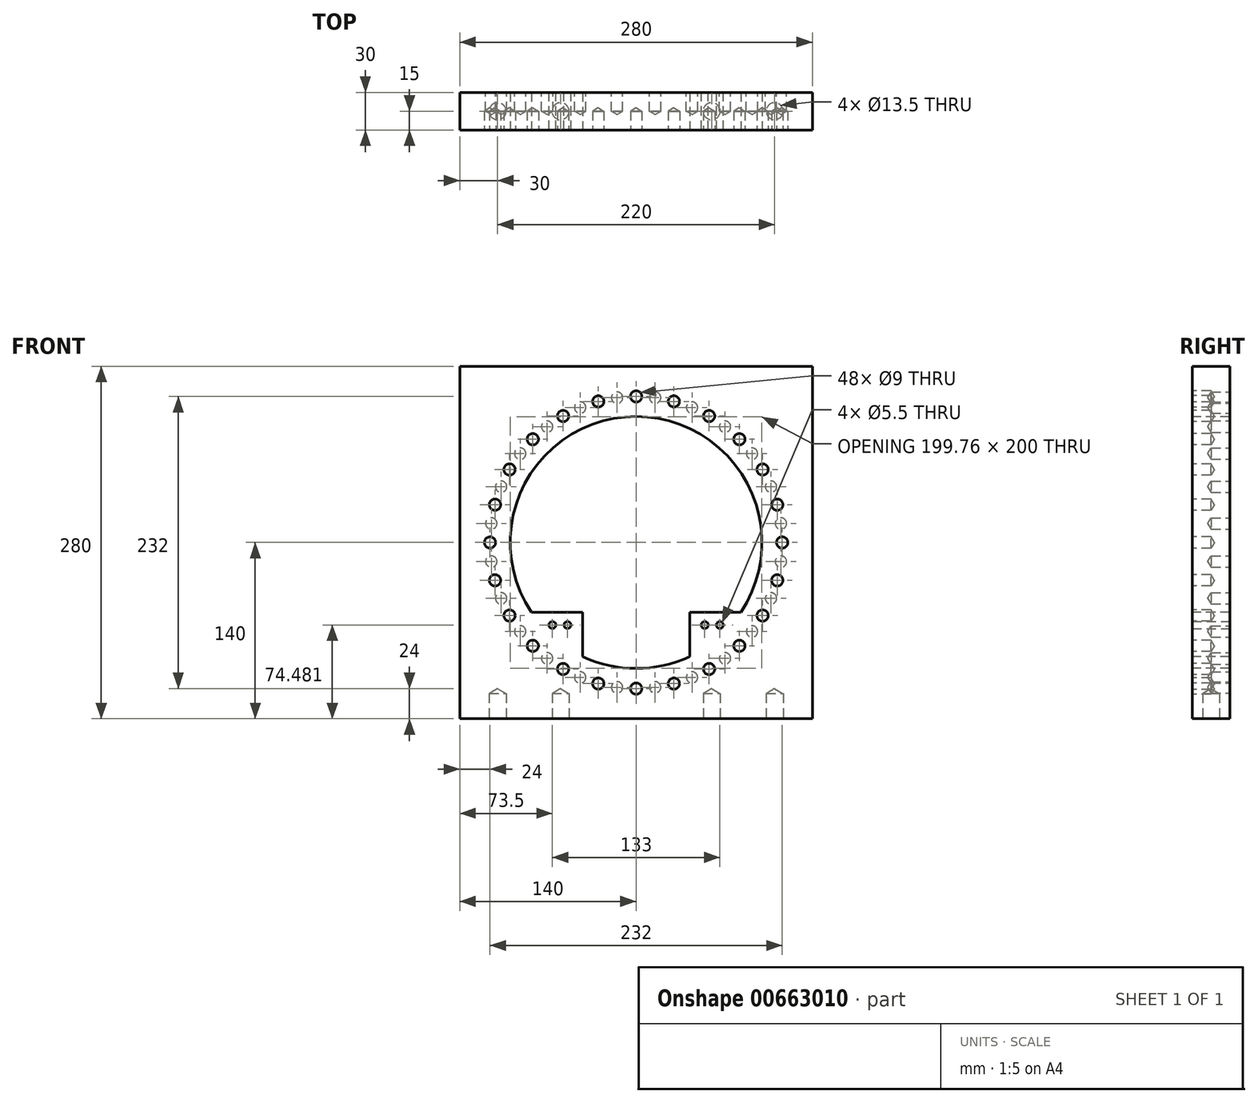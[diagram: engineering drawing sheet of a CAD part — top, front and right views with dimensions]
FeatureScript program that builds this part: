
annotation { "Feature Type Name" : "Feature", "Feature Type Description" : "" }
export const myFeature = defineFeature(function(context is Context, id is Id, definition is map)
    precondition{}
    {
        {
            var Q0;
            Q0=qCreatedBy(makeId("Front.planeOp"),FACE);
            var sketch = newSketch(context, id + "F0", { "sketchPlane" : qUnion([Q0])});
            skLineSegment(sketch, "E0.bottom", {"start": v(140, -140) * mm, "end": v(-140, -140) * mm});
            skLineSegment(sketch, "E0.top", {"start": v(140, 140) * mm, "end": v(-140, 140) * mm});
            skLineSegment(sketch, "E0.left", {"start": v(140, -140) * mm, "end": v(140, 140) * mm});
            skLineSegment(sketch, "E0.right", {"start": v(-140, -140) * mm, "end": v(-140, 140) * mm});
            skPoint(sketch, "E0.middle", {"position": v(0, 0) * mm});
            skCircle(sketch, "E1", {"center": v(0, 0) * mm, "radius": 100 * mm});
            skCircle(sketch, "E2", {"center": v(0, 0) * mm, "radius": 127 * mm, "construction": true});
            skSolve(sketch);
        }
        {
            var Q0;
            Q0=makeQuery(id+"F0.imprint","IMPRINT",FACE,{"disambiguationData":[TD([[makeQuery(id+"F0.imprint","IMPRINT",EDGE,{"derivedFrom":sQuery(id+"F0.wireOp",EDGE,"E0.bottom")}),-1.0]])]});
            var Q1;
            Q1=makeQuery(id+"F0.imprint","IMPRINT",FACE,{"disambiguationData":[TD([[makeQuery(id+"F0.imprint","IMPRINT",EDGE,{"derivedFrom":sQuery(id+"F0.wireOp",EDGE,"E1")}),1.0]])]});
            extrude(context, id + "F1", {"entities" : qUnion([Q0, Q1]), "depth" : 30 * mm, "offsetDistance" : 25 * mm});
        }
        {
            var Q0;
            Q0=makeQuery(id+"F1.opExtrude","SWEPT_FACE",FACE,{"disambiguationData":[OSD([sQuery(id+"F0.wireOp",EDGE,"E0.bottom")])]});
            var sketch = newSketch(context, id + "F2", { "sketchPlane" : qUnion([Q0])});
            skPoint(sketch, "E3", {"position": v(-110, 15) * mm});
            skPoint(sketch, "E3.positionSnap0", {"position": v(-140, 15) * mm});
            skPoint(sketch, "E4", {"position": v(110, 15) * mm});
            skPoint(sketch, "E5", {"position": v(60, 15) * mm});
            skPoint(sketch, "E6", {"position": v(-60, 15) * mm});
            skLineSegment(sketch, "E7", {"start": v(140, 15) * mm, "end": v(110, 15) * mm, "construction": true});
            skLineSegment(sketch, "E8", {"start": v(110, 15) * mm, "end": v(60, 15) * mm, "construction": true});
            skLineSegment(sketch, "E9", {"start": v(60, 15) * mm, "end": v(-60, 15) * mm, "construction": true});
            skLineSegment(sketch, "E10", {"start": v(-60, 15) * mm, "end": v(-110, 15) * mm, "construction": true});
            skLineSegment(sketch, "E11", {"start": v(-110, 15) * mm, "end": v(-140, 15) * mm, "construction": true});
            skSolve(sketch);
        }
        {
            var Q0;
            Q0=sQuery(id+"F2.wireOp",VERTEX,"E4");
            var Q1;
            Q1=sQuery(id+"F2.wireOp",VERTEX,"E5");
            var Q2;
            Q2=sQuery(id+"F2.wireOp",VERTEX,"E6");
            var Q3;
            Q3=sQuery(id+"F2.wireOp",VERTEX,"E3");
            var Q4;
            Q4=makeQuery(id+"F1.opExtrude","SWEPT_BODY",BODY,{"disambiguationData":[OSD([sQuery(id+"F0.wireOp",EDGE,"E0.bottom"),sQuery(id+"F0.wireOp",EDGE,"E0.top"),sQuery(id+"F0.wireOp",EDGE,"E0.left"),sQuery(id+"F0.wireOp",EDGE,"E0.right"),sQuery(id+"F0.wireOp",EDGE,"E1")])]});
            hole(context, id + "F3", {"style" : HoleStyle.SIMPLE, "endStyle" : HoleEndStyle.BLIND, "standardTappedOrClearance" : lookupTablePath({ "fit" : "Normal", "standard" : "ISO", "size" : "M12", "type" : "Clearance" }), "standardBlindInLast" : lookupTablePath({ "fit" : "Normal", "standard" : "ISO", "engagement" : "75%", "pitch" : "1.75 mm", "size" : "M12", "type" : "Clearance & tapped" }), "holeDiameter" : 13.5 * mm, "majorDiameter" : 5 * mm, "holeDepth" : 20 * mm, "isTappedThrough" : true, "tappedDepth" : 12 * mm, "tapClearance" : 3, "locations" : qUnion([Q0, Q1, Q2, Q3]), "scope" : qUnion([Q4])});
        }
        {
            var Q0;
            Q0=makeQuery(id+"F1.opExtrude","CAP_FACE",FACE,{"disambiguationData":[OSD([sQuery(id+"F0.wireOp",EDGE,"E0.bottom"),sQuery(id+"F0.wireOp",EDGE,"E0.top"),sQuery(id+"F0.wireOp",EDGE,"E0.left"),sQuery(id+"F0.wireOp",EDGE,"E0.right")])],"isStart":false});
            var sketch = newSketch(context, id + "F4", { "sketchPlane" : qUnion([Q0])});
            skLineSegment(sketch, "E12", {"start": v(42.5, -90.52) * mm, "end": v(42.5, -55.52) * mm});
            skLineSegment(sketch, "E13", {"start": v(42.5, -55.52) * mm, "end": v(83.17, -55.52) * mm});
            skLineSegment(sketch, "E14", {"start": v(-83.17, -55.52) * mm, "end": v(-42.5, -55.52) * mm});
            skLineSegment(sketch, "E15", {"start": v(-42.5, -55.52) * mm, "end": v(42.5, -55.52) * mm, "construction": true});
            skLineSegment(sketch, "E16", {"start": v(-42.5, -55.52) * mm, "end": v(-42.5, -90.52) * mm});
            skLineSegment(sketch, "E17", {"start": v(0, -55.52) * mm, "end": v(0, -85.52) * mm, "construction": true});
            skLineSegment(sketch, "E18", {"start": v(-42.5, -85.52) * mm, "end": v(0, -85.52) * mm, "construction": true});
            skLineSegment(sketch, "E19", {"start": v(0, -85.52) * mm, "end": v(42.5, -85.52) * mm, "construction": true});
            skArc(sketch, "E20", {"start": v(-42.5, -90.52) * mm, "mid": v(0, -100) * mm, "end": v(42.5, -90.52) * mm});
            skArc(sketch, "E21", {"start": v(42.5, -90.52) * mm, "mid": v(65.23, -75.8) * mm, "end": v(83.17, -55.52) * mm, "construction": true});
            skLineSegment(sketch, "E22", {"start": v(83.17, -55.52) * mm, "end": v(83.17, -55.52) * mm});
            skArc(sketch, "E23", {"start": v(-83.17, -55.52) * mm, "mid": v(-65.23, -75.8) * mm, "end": v(-42.5, -90.52) * mm, "construction": true});
            skLineSegment(sketch, "E24", {"start": v(0, 0) * mm, "end": v(0, -55.52) * mm, "construction": true});
            skArc(sketch, "E25", {"start": v(83.17, -55.52) * mm, "mid": v(0, 100) * mm, "end": v(-83.17, -55.52) * mm});
            skSolve(sketch);
        }
        {
            var Q0;
            Q0=makeQuery(id+"F4.imprint","IMPRINT",FACE,{"disambiguationData":[TD([[makeQuery(id+"F4.imprint","IMPRINT",EDGE,{"derivedFrom":sQuery(id+"F4.wireOp",EDGE,"E12")}),1.0]])]});
            extrude(context, id + "F5", {"entities" : qUnion([Q0]), "operationType" : NewBodyOperationType.REMOVE, "endBound" : BoundingType.THROUGH_ALL, "oppositeDirection" : true, "depth" : 25 * mm, "offsetDistance" : 25 * mm});
        }
        {
            var Q0;
            Q0=makeQuery(id+"F1.opExtrude","CAP_FACE",FACE,{"disambiguationData":[OSD([sQuery(id+"F0.wireOp",EDGE,"E0.bottom"),sQuery(id+"F0.wireOp",EDGE,"E0.top"),sQuery(id+"F0.wireOp",EDGE,"E0.left"),sQuery(id+"F0.wireOp",EDGE,"E0.right")])],"isStart":false});
            var sketch = newSketch(context, id + "F6", { "sketchPlane" : qUnion([Q0])});
            skCircle(sketch, "E26", {"center": v(0, 0) * mm, "radius": 116 * mm, "construction": true});
            skPoint(sketch, "E27", {"position": v(0, 116) * mm});
            skPoint(sketch, "E28.1.0", {"position": v(-30.02, 112.05) * mm});
            skPoint(sketch, "E28.2.0", {"position": v(-58, 100.46) * mm});
            skPoint(sketch, "E28.3.0", {"position": v(-82.02, 82.02) * mm});
            skPoint(sketch, "E28.4.0", {"position": v(-100.46, 58) * mm});
            skPoint(sketch, "E28.5.0", {"position": v(-112.05, 30.02) * mm});
            skPoint(sketch, "E28.6.0", {"position": v(-116, 0) * mm});
            skPoint(sketch, "E28.7.0", {"position": v(-112.05, -30.02) * mm});
            skPoint(sketch, "E28.8.0", {"position": v(-100.46, -58) * mm});
            skPoint(sketch, "E28.9.0", {"position": v(-82.02, -82.02) * mm});
            skPoint(sketch, "E28.10.0", {"position": v(-58, -100.46) * mm});
            skPoint(sketch, "E28.11.0", {"position": v(-30.02, -112.05) * mm});
            skPoint(sketch, "E28.12.0", {"position": v(0, -116) * mm});
            skPoint(sketch, "E28.13.0", {"position": v(30.02, -112.05) * mm});
            skPoint(sketch, "E28.14.0", {"position": v(58, -100.46) * mm});
            skPoint(sketch, "E28.15.0", {"position": v(82.02, -82.02) * mm});
            skPoint(sketch, "E28.16.0", {"position": v(100.46, -58) * mm});
            skPoint(sketch, "E28.17.0", {"position": v(112.05, -30.02) * mm});
            skPoint(sketch, "E28.18.0", {"position": v(116, 0) * mm});
            skPoint(sketch, "E28.19.0", {"position": v(112.05, 30.02) * mm});
            skPoint(sketch, "E28.20.0", {"position": v(100.46, 58) * mm});
            skPoint(sketch, "E28.21.0", {"position": v(82.02, 82.02) * mm});
            skPoint(sketch, "E28.22.0", {"position": v(58, 100.46) * mm});
            skPoint(sketch, "E28.23.0", {"position": v(30.02, 112.05) * mm});
            skSolve(sketch);
        }
        {
            var Q0;
            Q0=sQuery(id+"F6.wireOp",VERTEX,"E27");
            var Q1;
            Q1=sQuery(id+"F6.wireOp",VERTEX,"E28.23.0");
            var Q2;
            Q2=sQuery(id+"F6.wireOp",VERTEX,"E28.22.0");
            var Q3;
            Q3=sQuery(id+"F6.wireOp",VERTEX,"E28.21.0");
            var Q4;
            Q4=sQuery(id+"F6.wireOp",VERTEX,"E28.20.0");
            var Q5;
            Q5=sQuery(id+"F6.wireOp",VERTEX,"E28.19.0");
            var Q6;
            Q6=sQuery(id+"F6.wireOp",VERTEX,"E28.18.0");
            var Q7;
            Q7=sQuery(id+"F6.wireOp",VERTEX,"E28.17.0");
            var Q8;
            Q8=sQuery(id+"F6.wireOp",VERTEX,"E28.16.0");
            var Q9;
            Q9=sQuery(id+"F6.wireOp",VERTEX,"E28.15.0");
            var Q10;
            Q10=sQuery(id+"F6.wireOp",VERTEX,"E28.14.0");
            var Q11;
            Q11=sQuery(id+"F6.wireOp",VERTEX,"E28.13.0");
            var Q12;
            Q12=sQuery(id+"F6.wireOp",VERTEX,"E28.12.0");
            var Q13;
            Q13=sQuery(id+"F6.wireOp",VERTEX,"E28.11.0");
            var Q14;
            Q14=sQuery(id+"F6.wireOp",VERTEX,"E28.10.0");
            var Q15;
            Q15=sQuery(id+"F6.wireOp",VERTEX,"E28.9.0");
            var Q16;
            Q16=sQuery(id+"F6.wireOp",VERTEX,"E28.8.0");
            var Q17;
            Q17=sQuery(id+"F6.wireOp",VERTEX,"E28.7.0");
            var Q18;
            Q18=sQuery(id+"F6.wireOp",VERTEX,"E28.6.0");
            var Q19;
            Q19=sQuery(id+"F6.wireOp",VERTEX,"E28.5.0");
            var Q20;
            Q20=sQuery(id+"F6.wireOp",VERTEX,"E28.4.0");
            var Q21;
            Q21=sQuery(id+"F6.wireOp",VERTEX,"E28.3.0");
            var Q22;
            Q22=sQuery(id+"F6.wireOp",VERTEX,"E28.2.0");
            var Q23;
            Q23=sQuery(id+"F6.wireOp",VERTEX,"E28.1.0");
            var Q24;
            Q24=makeQuery(id+"F1.opExtrude","SWEPT_BODY",BODY,{"disambiguationData":[OSD([sQuery(id+"F0.wireOp",EDGE,"E0.bottom"),sQuery(id+"F0.wireOp",EDGE,"E0.top"),sQuery(id+"F0.wireOp",EDGE,"E0.left"),sQuery(id+"F0.wireOp",EDGE,"E0.right")])]});
            hole(context, id + "F7", {"style" : HoleStyle.SIMPLE, "endStyle" : HoleEndStyle.BLIND, "standardTappedOrClearance" : lookupTablePath({ "fit" : "Normal", "standard" : "ISO", "size" : "M8", "type" : "Clearance" }), "standardBlindInLast" : lookupTablePath({ "fit" : "Normal", "standard" : "ISO", "engagement" : "75%", "pitch" : "1.25 mm", "size" : "M8", "type" : "Clearance & tapped" }), "holeDiameter" : 9 * mm, "majorDiameter" : 5 * mm, "holeDepth" : 15 * mm, "isTappedThrough" : true, "tappedDepth" : 12 * mm, "tapClearance" : 3, "locations" : qUnion([Q0, Q1, Q2, Q3, Q4, Q5, Q6, Q7, Q8, Q9, Q10, Q11, Q12, Q13, Q14, Q15, Q16, Q17, Q18, Q19, Q20, Q21, Q22, Q23]), "scope" : qUnion([Q24])});
        }
        {
            var Q0;
            Q0=makeQuery(id+"F1.opExtrude","CAP_FACE",FACE,{"disambiguationData":[OSD([sQuery(id+"F0.wireOp",EDGE,"E0.bottom"),sQuery(id+"F0.wireOp",EDGE,"E0.top"),sQuery(id+"F0.wireOp",EDGE,"E0.left"),sQuery(id+"F0.wireOp",EDGE,"E0.right")])],"isStart":true});
            var sketch = newSketch(context, id + "F8", { "sketchPlane" : qUnion([Q0])});
            skCircle(sketch, "E29", {"center": v(0, 0) * mm, "radius": 116 * mm, "construction": true});
            skPoint(sketch, "E30", {"position": v(15.14, 115) * mm});
            skLineSegment(sketch, "E31", {"start": v(15.14, 115) * mm, "end": v(0, 0) * mm, "construction": true});
            skPoint(sketch, "E32.1.0", {"position": v(-15.14, 115) * mm});
            skPoint(sketch, "E32.2.0", {"position": v(-44.4, 107.17) * mm});
            skPoint(sketch, "E32.3.0", {"position": v(-70.62, 92.03) * mm});
            skPoint(sketch, "E32.4.0", {"position": v(-92.03, 70.62) * mm});
            skPoint(sketch, "E32.5.0", {"position": v(-107.17, 44.4) * mm});
            skPoint(sketch, "E32.6.0", {"position": v(-115, 15.14) * mm});
            skPoint(sketch, "E32.7.0", {"position": v(-115, -15.14) * mm});
            skPoint(sketch, "E32.8.0", {"position": v(-107.17, -44.4) * mm});
            skPoint(sketch, "E32.9.0", {"position": v(-92.03, -70.62) * mm});
            skPoint(sketch, "E32.10.0", {"position": v(-70.62, -92.03) * mm});
            skPoint(sketch, "E32.11.0", {"position": v(-44.4, -107.17) * mm});
            skPoint(sketch, "E32.12.0", {"position": v(-15.14, -115) * mm});
            skPoint(sketch, "E32.13.0", {"position": v(15.14, -115) * mm});
            skPoint(sketch, "E32.14.0", {"position": v(44.4, -107.17) * mm});
            skPoint(sketch, "E32.15.0", {"position": v(70.62, -92.03) * mm});
            skPoint(sketch, "E32.16.0", {"position": v(92.03, -70.62) * mm});
            skPoint(sketch, "E32.17.0", {"position": v(107.17, -44.4) * mm});
            skPoint(sketch, "E32.18.0", {"position": v(115, -15.14) * mm});
            skPoint(sketch, "E32.19.0", {"position": v(115, 15.14) * mm});
            skPoint(sketch, "E32.20.0", {"position": v(107.17, 44.4) * mm});
            skPoint(sketch, "E32.21.0", {"position": v(92.03, 70.62) * mm});
            skPoint(sketch, "E32.22.0", {"position": v(70.62, 92.03) * mm});
            skPoint(sketch, "E32.23.0", {"position": v(44.4, 107.17) * mm});
            skSolve(sketch);
        }
        {
            var Q0;
            Q0=sQuery(id+"F8.wireOp",VERTEX,"E30");
            var Q1;
            Q1=sQuery(id+"F8.wireOp",VERTEX,"E32.23.0");
            var Q2;
            Q2=sQuery(id+"F8.wireOp",VERTEX,"E32.22.0");
            var Q3;
            Q3=sQuery(id+"F8.wireOp",VERTEX,"E32.21.0");
            var Q4;
            Q4=sQuery(id+"F8.wireOp",VERTEX,"E32.20.0");
            var Q5;
            Q5=sQuery(id+"F8.wireOp",VERTEX,"E32.19.0");
            var Q6;
            Q6=sQuery(id+"F8.wireOp",VERTEX,"E32.18.0");
            var Q7;
            Q7=sQuery(id+"F8.wireOp",VERTEX,"E32.17.0");
            var Q8;
            Q8=sQuery(id+"F8.wireOp",VERTEX,"E32.16.0");
            var Q9;
            Q9=sQuery(id+"F8.wireOp",VERTEX,"E32.15.0");
            var Q10;
            Q10=sQuery(id+"F8.wireOp",VERTEX,"E32.14.0");
            var Q11;
            Q11=sQuery(id+"F8.wireOp",VERTEX,"E32.13.0");
            var Q12;
            Q12=sQuery(id+"F8.wireOp",VERTEX,"E32.12.0");
            var Q13;
            Q13=sQuery(id+"F8.wireOp",VERTEX,"E32.11.0");
            var Q14;
            Q14=sQuery(id+"F8.wireOp",VERTEX,"E32.10.0");
            var Q15;
            Q15=sQuery(id+"F8.wireOp",VERTEX,"E32.9.0");
            var Q16;
            Q16=sQuery(id+"F8.wireOp",VERTEX,"E32.8.0");
            var Q17;
            Q17=sQuery(id+"F8.wireOp",VERTEX,"E32.7.0");
            var Q18;
            Q18=sQuery(id+"F8.wireOp",VERTEX,"E32.6.0");
            var Q19;
            Q19=sQuery(id+"F8.wireOp",VERTEX,"E32.5.0");
            var Q20;
            Q20=sQuery(id+"F8.wireOp",VERTEX,"E32.4.0");
            var Q21;
            Q21=sQuery(id+"F8.wireOp",VERTEX,"E32.3.0");
            var Q22;
            Q22=sQuery(id+"F8.wireOp",VERTEX,"E32.2.0");
            var Q23;
            Q23=sQuery(id+"F8.wireOp",VERTEX,"E32.1.0");
            var Q24;
            Q24=makeQuery(id+"F1.opExtrude","SWEPT_BODY",BODY,{"disambiguationData":[OSD([sQuery(id+"F0.wireOp",EDGE,"E0.bottom"),sQuery(id+"F0.wireOp",EDGE,"E0.top"),sQuery(id+"F0.wireOp",EDGE,"E0.left"),sQuery(id+"F0.wireOp",EDGE,"E0.right")])]});
            hole(context, id + "F9", {"style" : HoleStyle.SIMPLE, "endStyle" : HoleEndStyle.BLIND, "standardTappedOrClearance" : lookupTablePath({ "fit" : "Normal", "standard" : "ISO", "size" : "M8", "type" : "Clearance" }), "standardBlindInLast" : lookupTablePath({ "fit" : "Normal", "standard" : "ISO", "engagement" : "75%", "pitch" : "1.25 mm", "size" : "M8", "type" : "Clearance & tapped" }), "holeDiameter" : 9 * mm, "majorDiameter" : 5 * mm, "holeDepth" : 15 * mm, "isTappedThrough" : true, "tappedDepth" : 12 * mm, "tapClearance" : 3, "locations" : qUnion([Q0, Q1, Q2, Q3, Q4, Q5, Q6, Q7, Q8, Q9, Q10, Q11, Q12, Q13, Q14, Q15, Q16, Q17, Q18, Q19, Q20, Q21, Q22, Q23]), "scope" : qUnion([Q24])});
        }
        {
            var Q0;
            Q0=makeQuery(id+"F1.opExtrude","CAP_FACE",FACE,{"disambiguationData":[OSD([sQuery(id+"F0.wireOp",EDGE,"E0.bottom"),sQuery(id+"F0.wireOp",EDGE,"E0.top"),sQuery(id+"F0.wireOp",EDGE,"E0.left"),sQuery(id+"F0.wireOp",EDGE,"E0.right")])],"isStart":true});
            var sketch = newSketch(context, id + "F10", { "sketchPlane" : qUnion([Q0])});
            skPoint(sketch, "E33", {"position": v(54.5, -65.52) * mm});
            skPoint(sketch, "E34", {"position": v(66.5, -65.52) * mm});
            skPoint(sketch, "E35", {"position": v(-54.5, -65.52) * mm});
            skPoint(sketch, "E36", {"position": v(-66.5, -65.52) * mm});
            skSolve(sketch);
        }
        {
            var Q0;
            Q0=sQuery(id+"F10.wireOp",VERTEX,"E33");
            var Q1;
            Q1=sQuery(id+"F10.wireOp",VERTEX,"E34");
            var Q2;
            Q2=sQuery(id+"F10.wireOp",VERTEX,"E36");
            var Q3;
            Q3=sQuery(id+"F10.wireOp",VERTEX,"E35");
            var Q4;
            Q4=makeQuery(id+"F1.opExtrude","SWEPT_BODY",BODY,{"disambiguationData":[OSD([sQuery(id+"F0.wireOp",EDGE,"E0.bottom"),sQuery(id+"F0.wireOp",EDGE,"E0.top"),sQuery(id+"F0.wireOp",EDGE,"E0.left"),sQuery(id+"F0.wireOp",EDGE,"E0.right")])]});
            hole(context, id + "F11", {"style" : HoleStyle.SIMPLE, "endStyle" : HoleEndStyle.THROUGH, "standardTappedOrClearance" : lookupTablePath({ "fit" : "Normal", "standard" : "ISO", "size" : "M5", "type" : "Clearance" }), "standardBlindInLast" : lookupTablePath({ "fit" : "Normal", "standard" : "ISO", "engagement" : "75%", "pitch" : "0.8 mm", "size" : "M5", "type" : "Clearance & tapped" }), "holeDiameter" : 5.5 * mm, "majorDiameter" : 5 * mm, "isTappedThrough" : true, "tappedDepth" : 12 * mm, "tapClearance" : 3, "locations" : qUnion([Q0, Q1, Q2, Q3]), "scope" : qUnion([Q4])});
        }
    });
